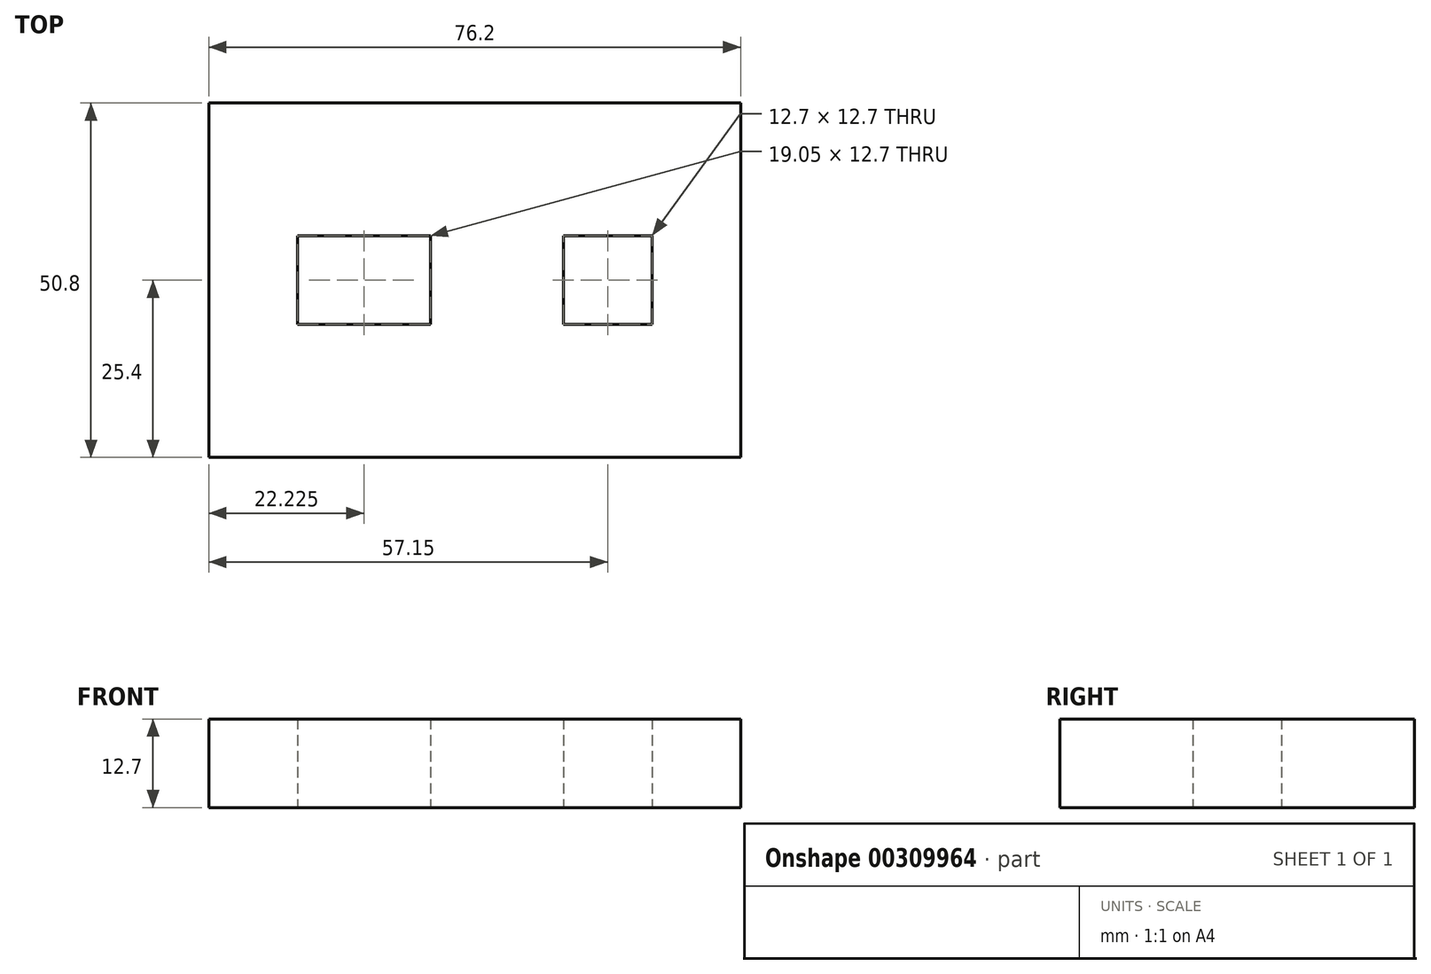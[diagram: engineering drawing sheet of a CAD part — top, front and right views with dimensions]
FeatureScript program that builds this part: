
annotation { "Feature Type Name" : "Feature", "Feature Type Description" : "" }
export const myFeature = defineFeature(function(context is Context, id is Id, definition is map)
    precondition{}
    {
        {
            var Q0;
            Q0=qCreatedBy(makeId("Top.planeOp"),FACE);
            var sketch = newSketch(context, id + "F0", { "sketchPlane" : qUnion([Q0])});
            skLineSegment(sketch, "E0.bottom", {"start": v(38.1, 25.4) * mm, "end": v(-38.1, 25.4) * mm});
            skLineSegment(sketch, "E0.top", {"start": v(38.1, -25.4) * mm, "end": v(-38.1, -25.4) * mm});
            skLineSegment(sketch, "E0.left", {"start": v(38.1, 25.4) * mm, "end": v(38.1, -25.4) * mm});
            skLineSegment(sketch, "E0.right", {"start": v(-38.1, 25.4) * mm, "end": v(-38.1, -25.4) * mm});
            skPoint(sketch, "E0.middle", {"position": v(0, 0) * mm});
            skLineSegment(sketch, "E1.bottom", {"start": v(-6.35, 6.35) * mm, "end": v(-25.4, 6.35) * mm});
            skLineSegment(sketch, "E1.top", {"start": v(-6.35, -6.35) * mm, "end": v(-25.4, -6.35) * mm});
            skLineSegment(sketch, "E1.left", {"start": v(-6.35, 6.35) * mm, "end": v(-6.35, -6.35) * mm});
            skLineSegment(sketch, "E1.right", {"start": v(-25.4, 6.35) * mm, "end": v(-25.4, -6.35) * mm});
            skPoint(sketch, "E1.middle", {"position": v(-15.87, 0) * mm});
            skLineSegment(sketch, "E2.bottom", {"start": v(25.4, 6.35) * mm, "end": v(12.7, 6.35) * mm});
            skLineSegment(sketch, "E2.top", {"start": v(25.4, -6.35) * mm, "end": v(12.7, -6.35) * mm});
            skLineSegment(sketch, "E2.left", {"start": v(25.4, 6.35) * mm, "end": v(25.4, -6.35) * mm});
            skLineSegment(sketch, "E2.right", {"start": v(12.7, 6.35) * mm, "end": v(12.7, -6.35) * mm});
            skPoint(sketch, "E2.middle", {"position": v(19.05, 0) * mm});
            skPoint(sketch, "E2.middle.positionSnap0", {"position": v(38.1, 0) * mm});
            skPoint(sketch, "E2.centerSnap0", {"position": v(38.1, 0) * mm});
            skSolve(sketch);
        }
        {
            var Q0;
            Q0=makeQuery(id+"F0.imprint","IMPRINT",FACE,{"disambiguationData":[TD([[makeQuery(id+"F0.imprint","IMPRINT",EDGE,{"derivedFrom":sQuery(id+"F0.wireOp",EDGE,"E0.bottom")}),1.0]])]});
            extrude(context, id + "F1", {"entities" : qUnion([Q0]), "depth" : 12.7 * mm});
        }
    });
